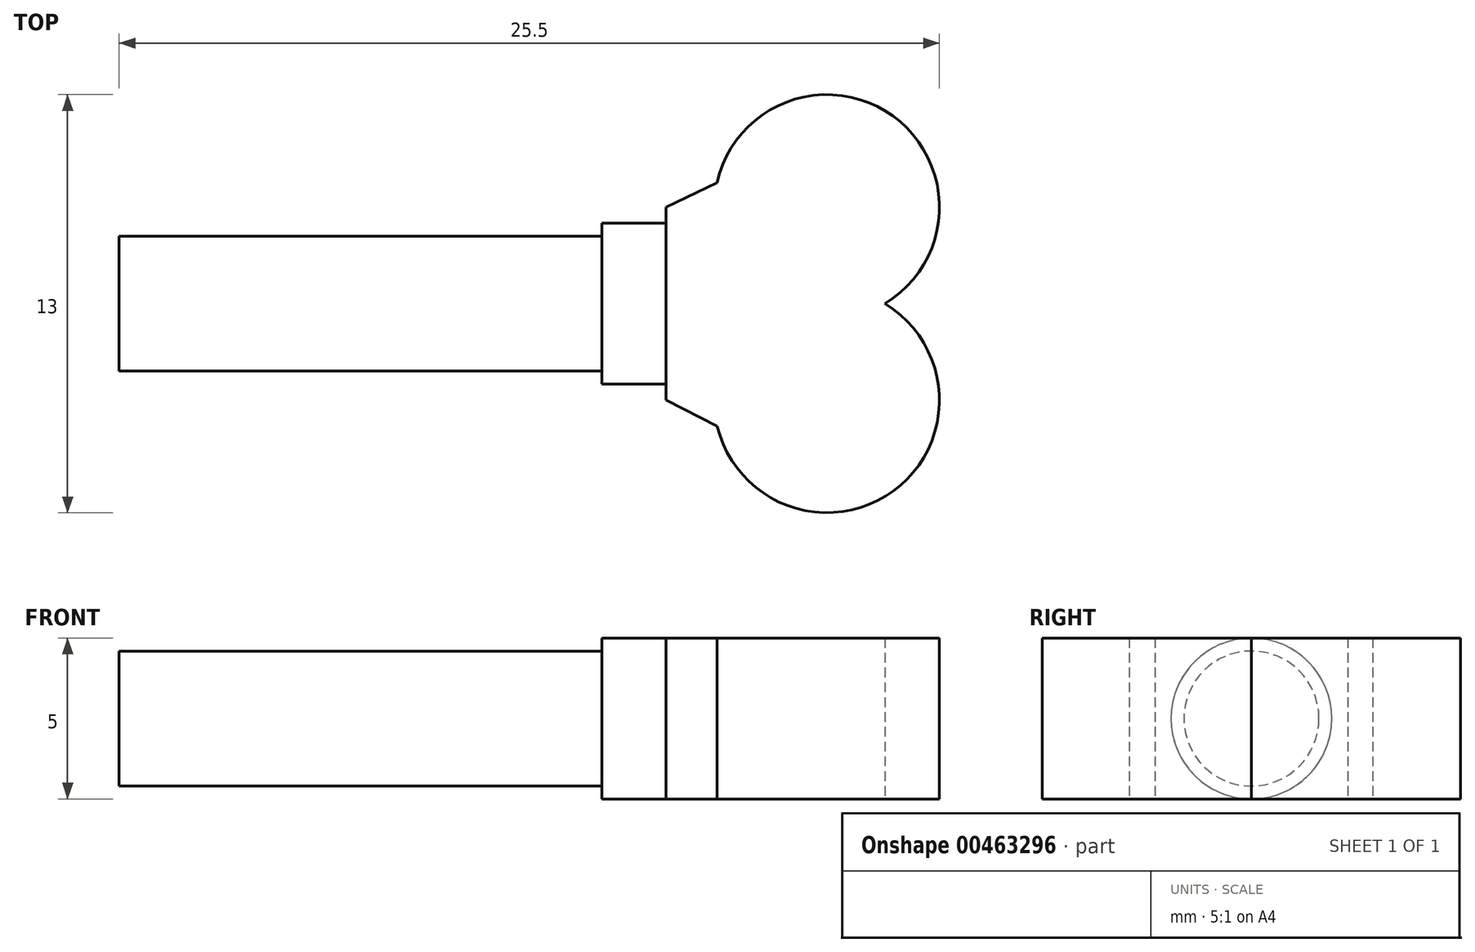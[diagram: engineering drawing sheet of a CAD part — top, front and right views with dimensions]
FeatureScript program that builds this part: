
annotation { "Feature Type Name" : "Feature", "Feature Type Description" : "" }
export const myFeature = defineFeature(function(context is Context, id is Id, definition is map)
    precondition{}
    {
        {
            var Q0;
            Q0=qCreatedBy(makeId("Top.planeOp"),FACE);
            var sketch = newSketch(context, id + "F0", { "sketchPlane" : qUnion([Q0])});
            skCircle(sketch, "E0", {"center": v(10, 6) * mm, "radius": 3.5 * mm});
            skCircle(sketch, "E1", {"center": v(10, 0) * mm, "radius": 3.5 * mm});
            skLineSegment(sketch, "E2", {"start": v(5, 3) * mm, "end": v(5, 6) * mm});
            skLineSegment(sketch, "E3", {"start": v(5, 3) * mm, "end": v(5, 0) * mm});
            skLineSegment(sketch, "E4", {"start": v(5, 6) * mm, "end": v(6.58, 6.77) * mm});
            skLineSegment(sketch, "E5", {"start": v(5, 0) * mm, "end": v(6.6, -0.8) * mm});
            skSolve(sketch);
        }
        {
            var Q0;
            {var subQ0=sQuery(id+"F0.wireOp",EDGE,"E1");var subQ1=sQuery(id+"F0.wireOp",EDGE,"E0");var subQ2=makeQuery(id+"F0.imprint","INTERSECT",VERTEX,{"disambiguationData":[OD(0.0)],"derivedFrom":[subQ1,subQ0]});Q0=makeQuery(id+"F0.imprint","IMPRINT",FACE,{"disambiguationData":[TD([[makeQuery(id+"F0.imprint","IMPRINT",EDGE,{"disambiguationData":[TD([[subQ2,1.0]])],"derivedFrom":subQ1}),1.0]])]});}
            var Q1;
            Q1=makeQuery(id+"F0.imprint","IMPRINT",FACE,{"disambiguationData":[TD([[makeQuery(id+"F0.imprint","IMPRINT",EDGE,{"derivedFrom":sQuery(id+"F0.wireOp",EDGE,"E2")}),-1.0]])]});
            var Q2;
            {var subQ0=sQuery(id+"F0.wireOp",EDGE,"E0");var subQ1=makeQuery(id+"F0.imprint","INTERSECT",VERTEX,{"derivedFrom":[subQ0,sQuery(id+"F0.wireOp",EDGE,"E4")]});Q2=makeQuery(id+"F0.imprint","IMPRINT",FACE,{"disambiguationData":[TD([[makeQuery(id+"F0.imprint","IMPRINT",EDGE,{"disambiguationData":[TD([[subQ1,-1.0]])],"derivedFrom":subQ0}),1.0]])]});}
            var Q3;
            {var subQ0=sQuery(id+"F0.wireOp",EDGE,"E1");var subQ1=sQuery(id+"F0.wireOp",EDGE,"E0");var subQ2=makeQuery(id+"F0.imprint","INTERSECT",VERTEX,{"disambiguationData":[OD(0.0)],"derivedFrom":[subQ1,subQ0]});Q3=makeQuery(id+"F0.imprint","IMPRINT",FACE,{"disambiguationData":[TD([[makeQuery(id+"F0.imprint","IMPRINT",EDGE,{"disambiguationData":[TD([[subQ2,1.0]])],"derivedFrom":subQ1}),-1.0]])]});}
            extrude(context, id + "F1", {"entities" : qUnion([Q0, Q1, Q2, Q3]), "endBound" : BoundingType.SYMMETRIC, "depth" : 5 * mm});
        }
        {
            var Q0;
            Q0=makeQuery(id+"F1.opExtrude","SWEPT_FACE",FACE,{"disambiguationData":[OSD([sQuery(id+"F0.wireOp",EDGE,"E2"),sQuery(id+"F0.wireOp",EDGE,"E3")])]});
            var sketch = newSketch(context, id + "F2", { "sketchPlane" : qUnion([Q0])});
            skLineSegment(sketch, "E6", {"start": v(0, 2.5) * mm, "end": v(-6, -2.5) * mm});
            skLineSegment(sketch, "E7", {"start": v(0, -2.5) * mm, "end": v(-6, 2.5) * mm});
            skCircle(sketch, "E8", {"center": v(-3, 0) * mm, "radius": 2.5 * mm});
            skSolve(sketch);
        }
        {
            var Q0;
            {var subQ0=sQuery(id+"F2.wireOp",EDGE,"E8");var subQ1=sQuery(id+"F2.wireOp",EDGE,"E6");var subQ2=makeQuery(id+"F2.imprint","INTERSECT",VERTEX,{"disambiguationData":[OD(0.0)],"derivedFrom":[subQ1,subQ0]});Q0=makeQuery(id+"F2.imprint","IMPRINT",FACE,{"disambiguationData":[TD([[makeQuery(id+"F2.imprint","IMPRINT",EDGE,{"disambiguationData":[TD([[subQ2,-1.0]])],"derivedFrom":subQ1}),1.0]])]});}
            var Q1;
            {var subQ0=sQuery(id+"F2.wireOp",EDGE,"E8");var subQ1=sQuery(id+"F2.wireOp",EDGE,"E6");var subQ2=makeQuery(id+"F2.imprint","INTERSECT",VERTEX,{"disambiguationData":[OD(0.0)],"derivedFrom":[subQ1,subQ0]});Q1=makeQuery(id+"F2.imprint","IMPRINT",FACE,{"disambiguationData":[TD([[makeQuery(id+"F2.imprint","IMPRINT",EDGE,{"disambiguationData":[TD([[subQ2,-1.0]])],"derivedFrom":subQ1}),-1.0]])]});}
            var Q2;
            {var subQ0=sQuery(id+"F2.wireOp",EDGE,"E7");var subQ1=sQuery(id+"F2.wireOp",EDGE,"E6");var subQ2=makeQuery(id+"F2.imprint","INTERSECT",VERTEX,{"derivedFrom":[subQ1,subQ0]});Q2=makeQuery(id+"F2.imprint","IMPRINT",FACE,{"disambiguationData":[TD([[makeQuery(id+"F2.imprint","IMPRINT",EDGE,{"disambiguationData":[TD([[subQ2,-1.0]])],"derivedFrom":subQ1}),1.0]])]});}
            var Q3;
            {var subQ0=sQuery(id+"F2.wireOp",EDGE,"E7");var subQ1=sQuery(id+"F2.wireOp",EDGE,"E6");var subQ2=makeQuery(id+"F2.imprint","INTERSECT",VERTEX,{"derivedFrom":[subQ1,subQ0]});Q3=makeQuery(id+"F2.imprint","IMPRINT",FACE,{"disambiguationData":[TD([[makeQuery(id+"F2.imprint","IMPRINT",EDGE,{"disambiguationData":[TD([[subQ2,-1.0]])],"derivedFrom":subQ1}),-1.0]])]});}
            extrude(context, id + "F3", {"entities" : qUnion([Q0, Q1, Q2, Q3]), "operationType" : NewBodyOperationType.ADD, "depth" : 2 * mm});
        }
        {
            var Q0;
            Q0=makeQuery(id+"F3.opExtrude","CAP_FACE",FACE,{"disambiguationData":[OSD([sQuery(id+"F2.wireOp",EDGE,"E8")])],"isStart":false});
            var sketch = newSketch(context, id + "F4", { "sketchPlane" : qUnion([Q0])});
            skCircle(sketch, "E9", {"center": v(-3, 0) * mm, "radius": 2.1 * mm});
            skSolve(sketch);
        }
        {
            var Q0;
            Q0=makeQuery(id+"F4.imprint","IMPRINT",FACE,{"disambiguationData":[TD([[makeQuery(id+"F4.imprint","IMPRINT",EDGE,{"derivedFrom":sQuery(id+"F4.wireOp",EDGE,"E9")}),1.0]])]});
            extrude(context, id + "F5", {"entities" : qUnion([Q0]), "operationType" : NewBodyOperationType.ADD, "depth" : 15 * mm});
        }
    });
